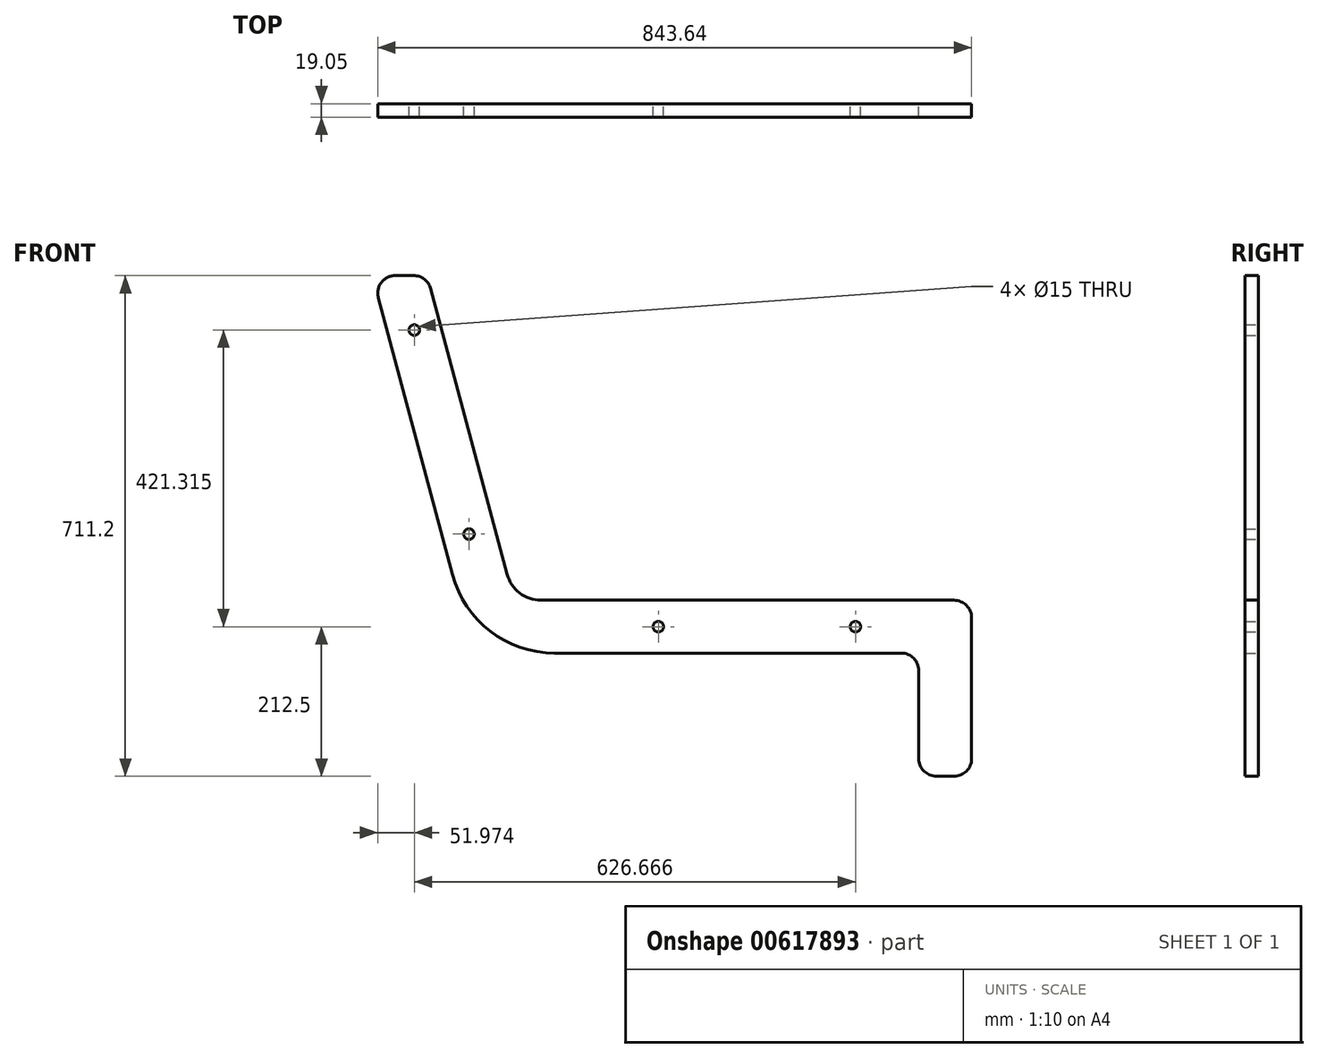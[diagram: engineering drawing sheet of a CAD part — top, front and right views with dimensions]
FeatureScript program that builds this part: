
annotation { "Feature Type Name" : "Feature", "Feature Type Description" : "" }
export const myFeature = defineFeature(function(context is Context, id is Id, definition is map)
    precondition{}
    {
        {
            var Q0;
            Q0=qCreatedBy(makeId("Front.planeOp"),FACE);
            var sketch = newSketch(context, id + "F0", { "sketchPlane" : qUnion([Q0])});
            skLineSegment(sketch, "E0", {"start": v(0, 25) * mm, "end": v(0, 225) * mm});
            skLineSegment(sketch, "E1", {"start": v(-25, 250) * mm, "end": v(-611.63, 250) * mm});
            skLineSegment(sketch, "E2", {"start": v(-659.93, 287.06) * mm, "end": v(-768.61, 692.67) * mm});
            skLineSegment(sketch, "E3", {"start": v(-792.76, 711.2) * mm, "end": v(-818.64, 711.2) * mm});
            skLineSegment(sketch, "E4", {"start": v(-842.8, 679.73) * mm, "end": v(-737.34, 286.18) * mm});
            skLineSegment(sketch, "E5", {"start": v(-592.45, 175) * mm, "end": v(-100, 175) * mm});
            skLineSegment(sketch, "E6", {"start": v(-75, 150) * mm, "end": v(-75, 25) * mm});
            skLineSegment(sketch, "E7", {"start": v(-50, 0) * mm, "end": v(-25, 0) * mm});
            skPoint(sketch, "E8.visualSharp", {"position": v(-650, 250) * mm});
            skArc(sketch, "E8.filletArc", {"start": v(-659.93, 287.06) * mm, "mid": v(-642.07, 260.33) * mm, "end": v(-611.63, 250) * mm});
            skPoint(sketch, "E9.visualSharp", {"position": v(-75, 175) * mm});
            skArc(sketch, "E9.filletArc", {"start": v(-75, 150) * mm, "mid": v(-82.32, 167.68) * mm, "end": v(-100, 175) * mm});
            skPoint(sketch, "E10.visualSharp", {"position": v(-707.55, 175) * mm});
            skArc(sketch, "E10.filletArc", {"start": v(-737.34, 286.18) * mm, "mid": v(-683.76, 206) * mm, "end": v(-592.45, 175) * mm});
            skPoint(sketch, "E11.visualSharp", {"position": v(0, 250) * mm});
            skArc(sketch, "E11.filletArc", {"start": v(0, 225) * mm, "mid": v(-7.32, 242.68) * mm, "end": v(-25, 250) * mm});
            skPoint(sketch, "E12.visualSharp", {"position": v(-851.22, 711.2) * mm});
            skArc(sketch, "E12.filletArc", {"start": v(-818.64, 711.2) * mm, "mid": v(-838.48, 701.42) * mm, "end": v(-842.8, 679.73) * mm});
            skPoint(sketch, "E13.visualSharp", {"position": v(-773.58, 711.2) * mm});
            skArc(sketch, "E13.filletArc", {"start": v(-768.61, 692.67) * mm, "mid": v(-777.54, 706.03) * mm, "end": v(-792.76, 711.2) * mm});
            skPoint(sketch, "E14.visualSharp", {"position": v(-75, 0) * mm});
            skArc(sketch, "E14.filletArc", {"start": v(-75, 25) * mm, "mid": v(-67.68, 7.32) * mm, "end": v(-50, 0) * mm});
            skPoint(sketch, "E15.visualSharp", {"position": v(0, 0) * mm});
            skArc(sketch, "E15.filletArc", {"start": v(-25, 0) * mm, "mid": v(-7.32, 7.32) * mm, "end": v(0, 25) * mm});
            skCircle(sketch, "E16", {"center": v(-445, 212.5) * mm, "radius": 7.5 * mm});
            skCircle(sketch, "E17", {"center": v(-165, 212.5) * mm, "radius": 7.5 * mm});
            skCircle(sketch, "E18", {"center": v(-791.67, 633.81) * mm, "radius": 7.5 * mm});
            skCircle(sketch, "E19", {"center": v(-714.02, 344.04) * mm, "radius": 7.5 * mm});
            skLineSegment(sketch, "E20", {"start": v(-445, 212.5) * mm, "end": v(-165, 212.5) * mm, "construction": true});
            skLineSegment(sketch, "E21", {"start": v(-165, 212.5) * mm, "end": v(0, 212.5) * mm, "construction": true});
            skLineSegment(sketch, "E22", {"start": v(-791.67, 633.81) * mm, "end": v(-714.02, 344.04) * mm, "construction": true});
            skLineSegment(sketch, "E23", {"start": v(-592.45, 175) * mm, "end": v(-1036.43, 175) * mm, "construction": true});
            skLineSegment(sketch, "E24", {"start": v(-714.02, 344.04) * mm, "end": v(-668.73, 175) * mm, "construction": true});
            skSolve(sketch);
        }
        {
            var Q0;
            Q0 = qSketchRegion(id + "F0", true);
            extrude(context, id + "F1", {"entities" : qUnion([Q0]), "depth" : (0.75 * 25.4) * mm, "offsetDistance" : 25 * mm});
        }
    });
